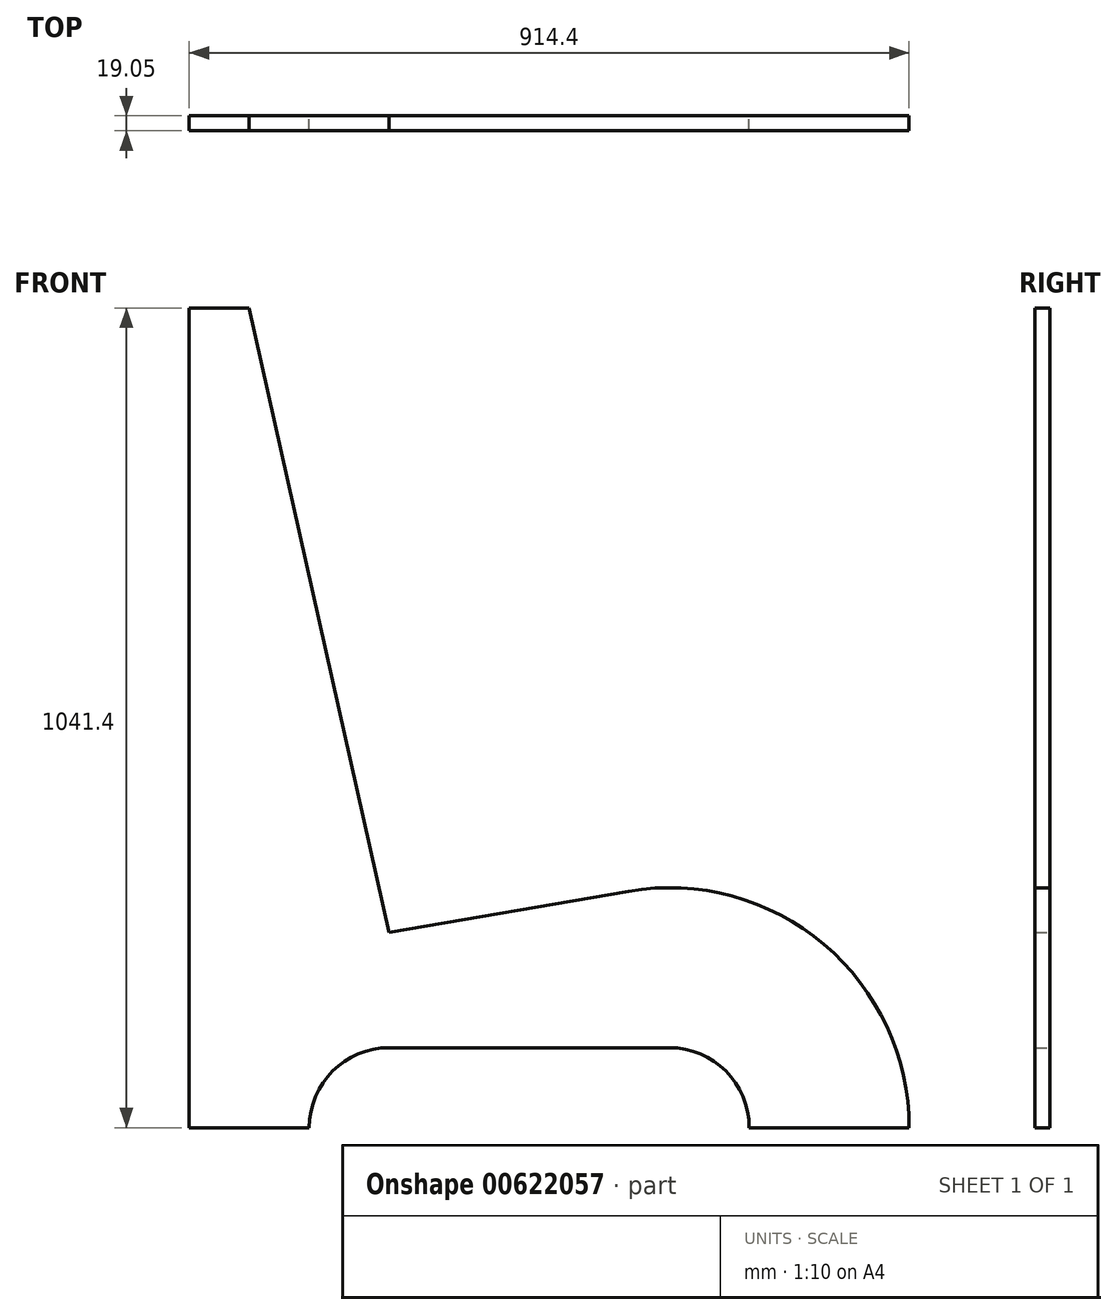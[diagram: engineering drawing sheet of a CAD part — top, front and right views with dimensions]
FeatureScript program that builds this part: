
annotation { "Feature Type Name" : "Feature", "Feature Type Description" : "" }
export const myFeature = defineFeature(function(context is Context, id is Id, definition is map)
    precondition{}
    {
        {
            var Q0;
            Q0=qCreatedBy(makeId("Front.planeOp"),FACE);
            var sketch = newSketch(context, id + "F0", { "sketchPlane" : qUnion([Q0])});
            skLineSegment(sketch, "E0", {"start": v(0, 0) * mm, "end": v(0, 1041.4) * mm});
            skLineSegment(sketch, "E1", {"start": v(0, 1041.4) * mm, "end": v(76.2, 1041.4) * mm});
            skLineSegment(sketch, "E2", {"start": v(76.2, 1041.4) * mm, "end": v(254, 248.29) * mm});
            skLineSegment(sketch, "E3", {"start": v(254, 248.29) * mm, "end": v(558.1, 300.42) * mm});
            skLineSegment(sketch, "E4", {"start": v(0, 0) * mm, "end": v(152.4, 0) * mm});
            skArc(sketch, "E5", {"start": v(254, 101.6) * mm, "mid": v(182.16, 71.84) * mm, "end": v(152.4, 0) * mm});
            skLineSegment(sketch, "E6", {"start": v(254, 101.6) * mm, "end": v(609.6, 101.6) * mm});
            skArc(sketch, "E7", {"start": v(711.2, 0) * mm, "mid": v(681.44, 71.84) * mm, "end": v(609.6, 101.6) * mm});
            skLineSegment(sketch, "E8", {"start": v(711.2, 0) * mm, "end": v(914.4, 0) * mm});
            skLineSegment(sketch, "E9", {"start": v(914.4, 0) * mm, "end": v(914.4, 0) * mm});
            skArc(sketch, "E10", {"start": v(558.1, 300.42) * mm, "mid": v(806.08, 233.02) * mm, "end": v(914.4, 0) * mm});
            skSolve(sketch);
        }
        {
            var Q0;
            Q0=makeQuery(id+"F0.imprint","IMPRINT",FACE,{"disambiguationData":[TD([[makeQuery(id+"F0.imprint","IMPRINT",EDGE,{"derivedFrom":sQuery(id+"F0.wireOp",EDGE,"E0")}),-1.0]])]});
            extrude(context, id + "F1", {"entities" : qUnion([Q0]), "depth" : 19.05 * mm, "offsetDistance" : 25.4 * mm});
        }
    });
